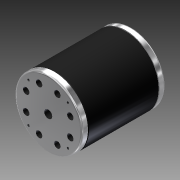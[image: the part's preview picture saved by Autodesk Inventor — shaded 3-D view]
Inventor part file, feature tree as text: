
AUTODESK INVENTOR PART (.ipt)
format: ipt  version: 2012 (Build 160160000, 160)  size: 202,240 bytes
history: native  units: in
note: dims shown in document units (in); Inventor stores cm internally (conversion verified against a paired STEP export)
features: sketch x5, extrude x4, chamfer x2, hole x1, mirror x1, fillet x1
ambient origin geometry x8: Origin, YZ Plane, XZ Plane, XY Plane, X Axis, Y Axis, Z Axis, Center Point
bodies: Solid1 (feature_tree)
feature tree (14):
  extrude  "Extrusion1"  Depth=4.5in TaperAngle=0.0deg
  chamfer  "Chamfer1"  Distance=0.0625in Angle=45.0deg
  chamfer  "Chamfer2"  Distance=0.0625in Angle=45.0deg
  extrude  "Front End"  Depth=1.5748in TaperAngle=360.0deg
  hole  "Mount Holes"  [1 undecoded]
  extrude  "Shaft Hole"  Depth=0.4in
  extrude  "Ventilation Holes"  Depth=1.5in
  mirror  "Mirror3"
  fillet  "Fillet1"  Radius=3.1496in
  sketch  "Sketch1"  dims[d0=4.25in d1=4.5in d2=0.0in d5=0.0625in d6=0.125in d7=45.0deg d8=0.0625in d9=0.125in d10=45.0deg]
  sketch  "Sketch3"  dims[d11=0.375in d12=0.0in d23=1.5748in d25=360.0deg]
  sketch  "Sketch5"  dims[d27=0.145in d28=0.5in d29=0.375in d30=0.25in d31=0.5635in d32=0.5in d33=0.8108in d34=0.5in]
  sketch  "Sketch6"  dims[d35=0.5in d36=0.0in d37=0.4in]
  sketch  "Sketch7"  dims[d38=22.5deg d39=1.5in d40=3.1496in d42=360.0deg d44=0.5in d45=0.0in d46=45.0deg d47=1.75in d48=0.125in]
note: 1 required parameter value undecoded (feature->parameter linkage not recoverable at this tier; creation-order binding heuristic only, values carry confidence <= 0.55)
